# Revit family: Bathtub-Freestanding-American_Standard-Kipling_Ovale-2767.034
name_source: partatom
category: Plumbing Fixtures
revit_build: Autodesk Revit 2014 (Build: 20130308_1515(x64)
units: mm (PartAtom-declared; Revit-internal decimal feet)

## types (1)
- 2767.034
    Assembly Code = D2010510
    CW Connection = Yes
    CWFU = 3
    Default Elevation = 0"
    Description = Kipling Ovale Freestanding Tub
    HW Connection = Yes
    HWFU = 3
    Height = 23 5/8"
    Installation Type = Floor Mount
    Length = 69 5/8"
    Manufacturer = American Standard
    Material = Acrylic-American Standard-020-High Gloss White
    Model = 2767.034
    Overflow Finish = Metal-American Standard-002-Polished Chrome
    Price = Prices may vary. Please consult Manufacturer Representative for most up-to-date price list.
    Product Documentation Link = https://www.americanstandard-us.com
    Product Page URL = https://www.americanstandard-us.com
    Shipping Weight = 110 lb
    Tub Finish = Acrylic-American Standard-020-High Gloss White
    URL = https://www.americanstandard-us.com
    Vent Connection = No
    WFU = 4
    Warranty Information = Limited Lifetime warranty
    Waste Connection = Yes
    Water Connection Diameter = 2 1/8"
    Width = 31 3/4"
    cUPC Compliant = Yes

## geometry (parser evidence)
native form markers: Sweep x1
no freeform markers — native parametric forms only
